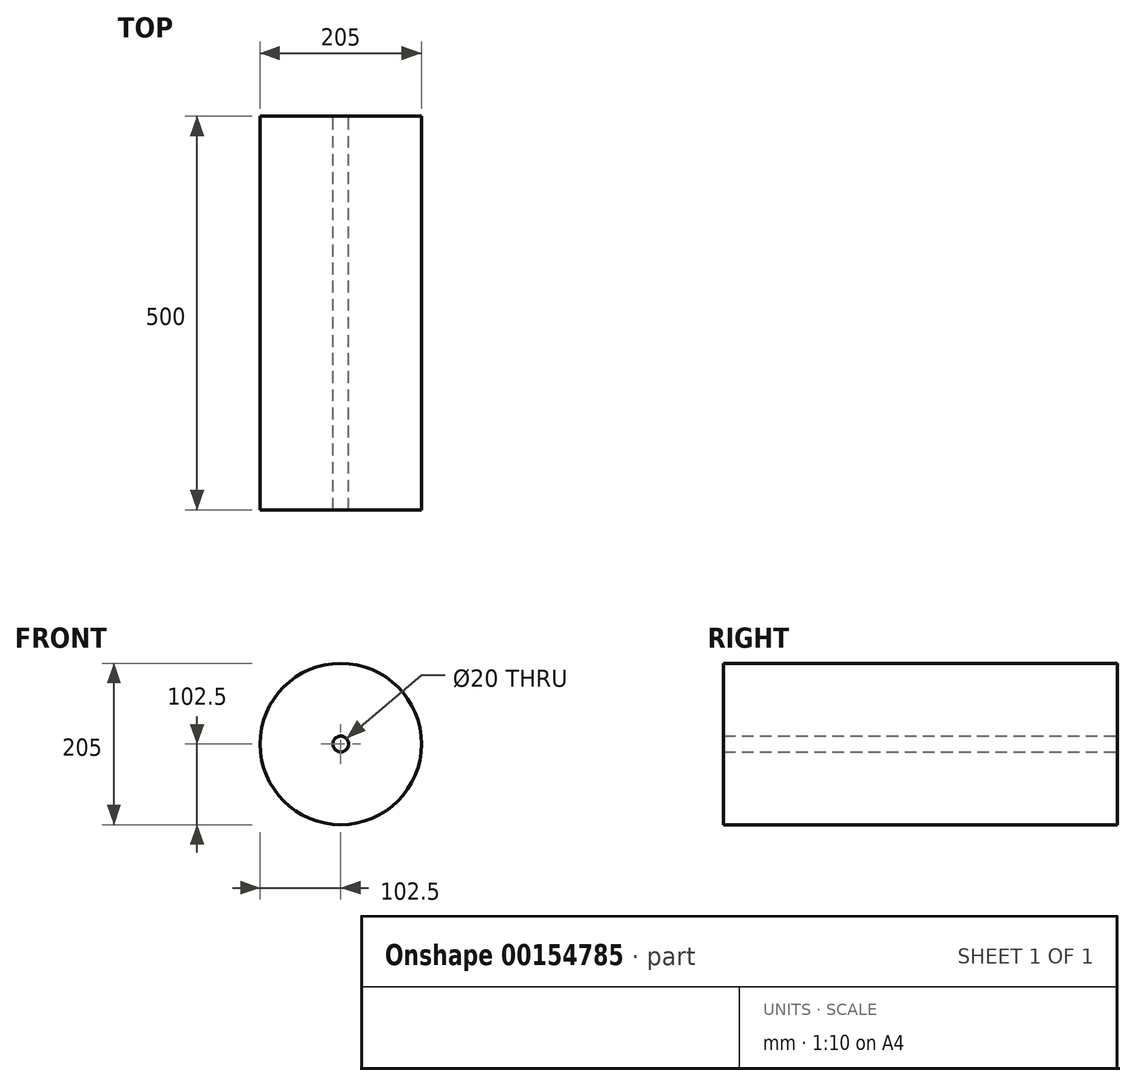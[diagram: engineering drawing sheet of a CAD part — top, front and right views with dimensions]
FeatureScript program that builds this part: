
annotation { "Feature Type Name" : "Feature", "Feature Type Description" : "" }
export const myFeature = defineFeature(function(context is Context, id is Id, definition is map)
    precondition{}
    {
        {
            var Q0;
            Q0=qCreatedBy(makeId("Front.planeOp"),FACE);
            var sketch = newSketch(context, id + "F0", { "sketchPlane" : qUnion([Q0])});
            skCircle(sketch, "E0", {"center": v(0, 0) * mm, "radius": 102.5 * mm});
            skCircle(sketch, "E1", {"center": v(0, 0) * mm, "radius": 10 * mm});
            skSolve(sketch);
        }
        {
            var Q0;
            Q0 = qSketchRegion(id + "F0", true);
            extrude(context, id + "F1", {"entities" : qUnion([Q0]), "depth" : 500 * mm});
        }
    });
